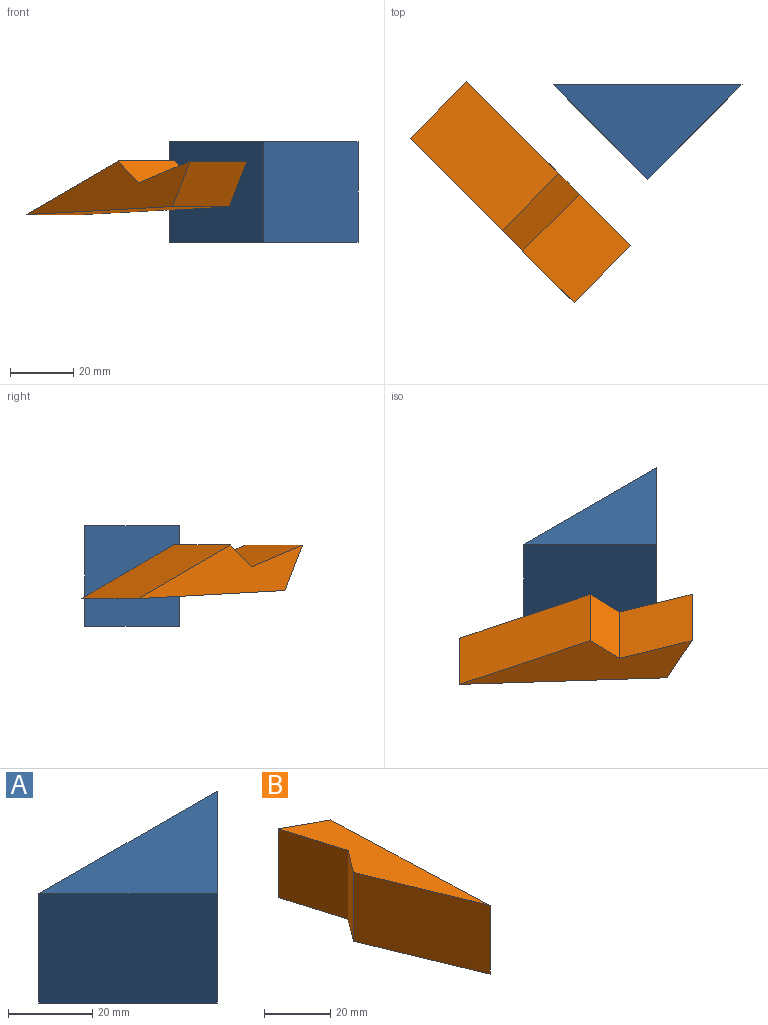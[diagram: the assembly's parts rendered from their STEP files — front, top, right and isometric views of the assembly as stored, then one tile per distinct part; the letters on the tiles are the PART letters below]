
ASSEMBLY  parts=2 mates=1
PART A: 5 faces, bbox 59.8x29.9x31.8 mm
  f0: plane 31.75x29.89mm, normal (-0.71,-0.71,0), area 1342.1mm2, adj f1,f2,f3,f4
  f1: plane 31.75x29.89mm, normal (0.71,-0.71,0), area 1342.1mm2, adj f0,f2,f3,f4
  f2: plane 59.78x31.75mm, normal (0,1,0), area 1898mm2, adj f0,f1,f3,f4
  f3: plane 59.78x29.89mm, normal (0,0,1), area 893.4mm2, adj f0,f1,f2
  f4: plane 59.78x29.89mm, normal (0,0,-1), area 893.4mm2, adj f0,f1,f2
PART B: 7 faces, bbox 17x73.5x25.4 mm
  f0: plane 25.4x9.25mm, normal (-0.8,0.6,0), area 293.6mm2, adj f1,f4,f5,f6
  f1: plane 41.27x25.4mm, normal (-0.92,-0.38,0), area 1133.7mm2, adj f0,f2,f5,f6
  f2: plane 65.69x25.4mm, normal (1,0.04,0), area 1669.7mm2, adj f1,f3,f5,f6
  f3: plane 25.4x14.4mm, normal (0.48,0.88,0), area 416.7mm2, adj f2,f4,f5,f6
  f4: plane 25.4x23.02mm, normal (-0.96,-0.29,0), area 610.5mm2, adj f0,f3,f5,f6
  f5: plane 73.54x16.99mm, normal (0,0,1), area 625.9mm2, adj f0,f1,f2,f3,f4
  f6: plane 73.54x16.99mm, normal (0,0,-1), area 625.9mm2, adj f0,f1,f2,f3,f4
PLACE A at identity fixed
PLACE B rot(axis=(0.68,0.28,-0.68),148.6deg) t=(-32.66,-2.76,-41.05)mm
MATE slider B.f6 <-> A.f0  axis (0.71,0.71,0) through (-32.65,-2.76,15.88)mm
